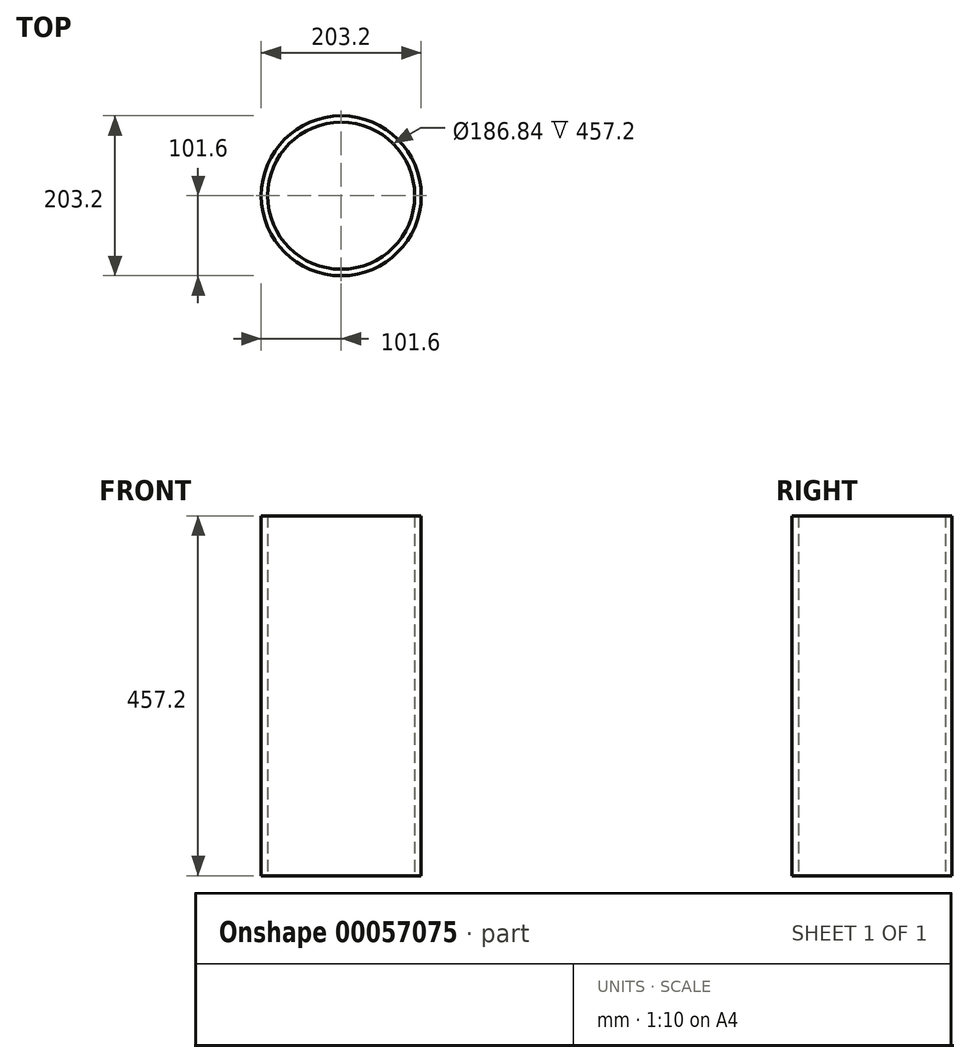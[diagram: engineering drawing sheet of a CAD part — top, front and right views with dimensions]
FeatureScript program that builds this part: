
annotation { "Feature Type Name" : "Feature", "Feature Type Description" : "" }
export const myFeature = defineFeature(function(context is Context, id is Id, definition is map)
    precondition{}
    {
        {
            var Q0;
            Q0=qCreatedBy(makeId("Top.planeOp"),FACE);
            var sketch = newSketch(context, id + "F0", { "sketchPlane" : qUnion([Q0])});
            skCircle(sketch, "E0", {"center": v(0, 0) * mm, "radius": 101.6 * mm});
            skCircle(sketch, "E1", {"center": v(0, 0) * mm, "radius": 93.42 * mm});
            skSolve(sketch);
        }
        {
            var Q0;
            Q0=makeQuery(id+"F0.imprint","IMPRINT",FACE,{"disambiguationData":[TD([[makeQuery(id+"F0.imprint","IMPRINT",EDGE,{"derivedFrom":sQuery(id+"F0.wireOp",EDGE,"E0")}),1.0]])]});
            extrude(context, id + "F1", {"entities" : qUnion([Q0]), "depth" : 457.2 * mm});
        }
    });
